# Revit family: 3-68 Spirit Pendant
name_source: partatom
category: Lighting Fixtures
revit_build: Autodesk Revit 2018 (Build: 20170223_1515(x64)
units: mm (PartAtom-declared; Revit-internal decimal feet)

## family parameters
Always vertical = Yes
Cut with Voids When Loaded = No
Host = Ceiling
Light Source = Yes
OmniClass Number = 23.80.70.11
OmniClass Title = Luminaries for Internal Lighting
Part Type = Normal
Room Calculation Point = No
Round Connector Dimension = Use Diameter
Shared = No

## types (16) — shared parameters
Color Filter = 16777215
Dimming Lamp Color Temperature Shift = <None>
Lamp = LED
Main Diffuser = Clear Bubble Glass
Manufacturer = Oxygen Lighting
Model = 3-68-xxxx-Spirit (Pendant)
Photometric Web File = Spirit 3-68-20.ies
References = Ref. 3 = 120 V / Ref. 37 = 277 V
Tilt Angle = 90.00°
Voltage = 120 V
Voltage Input = 120 V or 277 V - 50/60 Hz
Wattage Comments = 6.99 W at 120 V

## per-type parameters (varying)
| type | Metal Finish | URL |
| 3-68-15 - Black / Clear Bubble Glass | 15 - Black |  |
| 3-68-24 - Satin Nickel / Clear Bubble Glass | 24 - Satin Nickel |  |
| 3-68-2715 - Black / Clear Bubble Glass | 24 - Satin Nickel |  |
| 3-68-2740 - Aged Brass / Clear Bubble Glass | 40 - Aged Brass |  |
| 3-68-276 - White / Clear Bubble Glass | 6 - White |  |
| 3-68-3515 - Black / Clear Bubble Glass | 15 - Black |  |
| 3-68-3540 - Aged Brass / Clear Bubble Glass | 40 - Aged Brass |  |
| 3-68-356 - White / Clear Bubble Glass | 6 - White |  |
| 3-68-4015 - Black / Clear Bubble Glass | 40 - Aged Brass |  |
| 3-68-4024 - Satin Nickel / Clear Bubble Glass | 24 - Satin Nickel |  |
| 3-68-4040 - Aged Brass / Clear Bubble Glass | 40 - Aged Brass |  |
| 3-68-406 - White / Clear Bubble Glass | 6 - White |  |
| 3-68-6 - White / Clear Bubble Glass | 6 - White |  |
| 3-68-40 - Aged Brass / Clear Bubble Glass | 40 - Aged Brass |  |
| 3-68-2724 - Satin Nickel / Clear Bubble Glass | 24 - Satin Nickel |  |
| 3-68-3524 - Satin Nickel / Clear Bubble Glass | 24 - Satin Nickel | www.oxygenlighting.com |

## geometry (parser evidence)
native form markers: Sweep x2
no freeform markers — native parametric forms only
